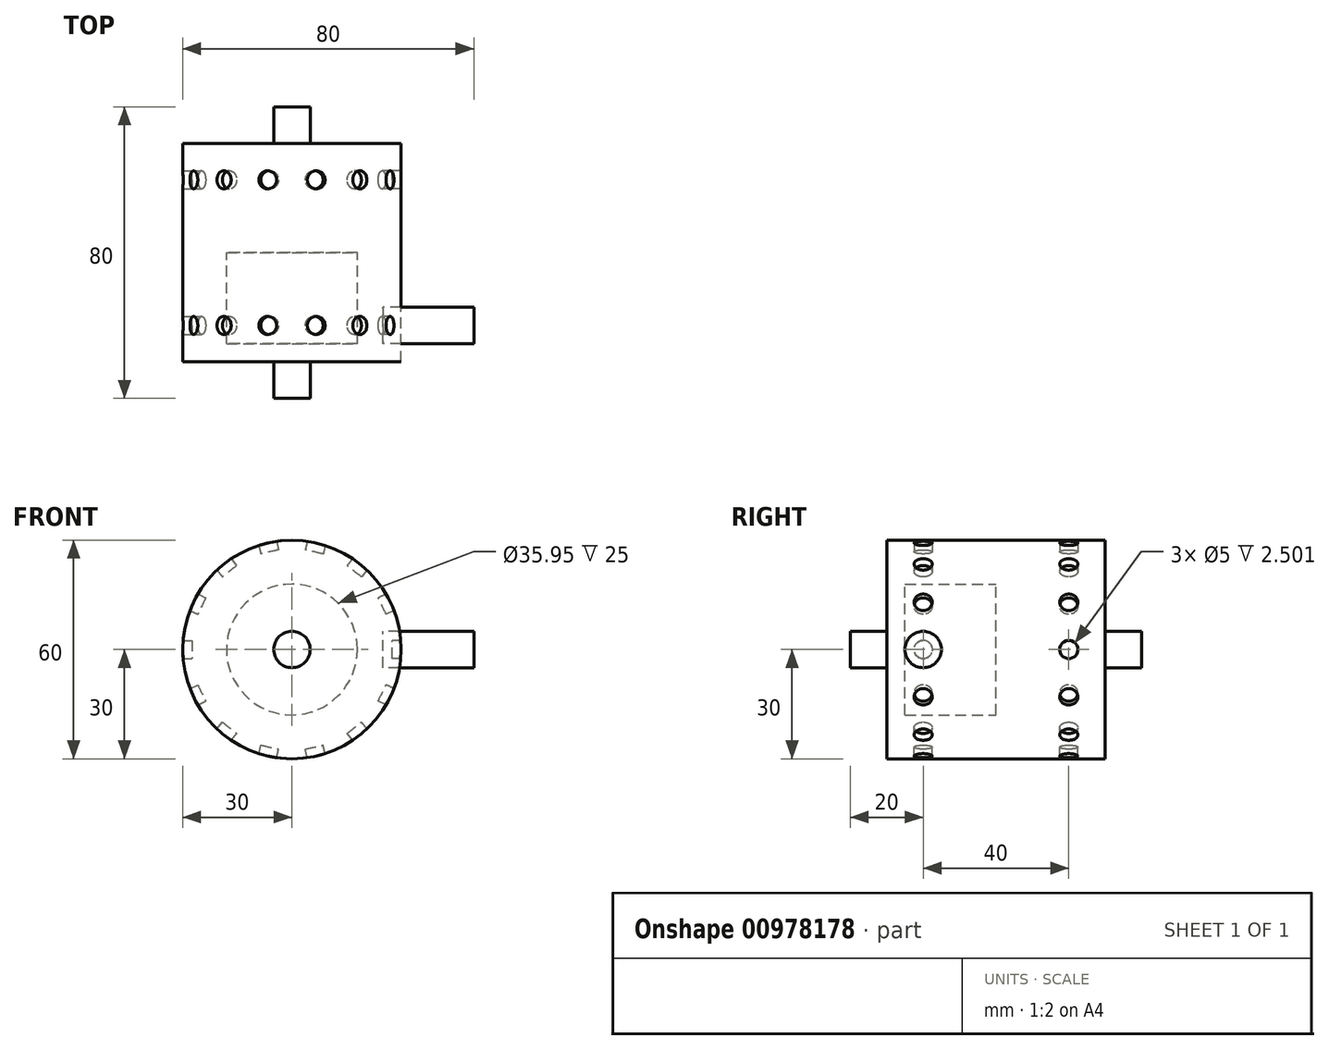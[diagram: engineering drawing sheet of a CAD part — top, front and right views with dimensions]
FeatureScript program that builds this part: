
annotation { "Feature Type Name" : "Feature", "Feature Type Description" : "" }
export const myFeature = defineFeature(function(context is Context, id is Id, definition is map)
    precondition{}
    {
        {
            var Q0;
            Q0=qCreatedBy(makeId("Front.planeOp"),FACE);
            var sketch = newSketch(context, id + "F0", { "sketchPlane" : qUnion([Q0])});
            skCircle(sketch, "E0", {"center": v(0, 0) * mm, "radius": 30 * mm});
            skLineSegment(sketch, "E1", {"start": v(72.87, 0) * mm, "end": v(-75.42, 0) * mm, "construction": true});
            skLineSegment(sketch, "E2", {"start": v(0, -74.84) * mm, "end": v(0, 74.05) * mm, "construction": true});
            skSolve(sketch);
        }
        {
            var Q0;
            Q0 = qSketchRegion(id + "F0", true);
            extrude(context, id + "F1", {"entities" : qUnion([Q0]), "endBound" : BoundingType.SYMMETRIC, "depth" : 60 * mm, "offsetDistance" : 25 * mm});
        }
        {
            var Q0;
            Q0=qCreatedBy(makeId("Right.planeOp"),FACE);
            cPlane(context, id + "F2", {"entities" : qUnion([Q0]), "cplaneType" : CPlaneType.OFFSET, "offset" : 25 * mm, "width" : 150 * mm, "height" : 150 * mm});
        }
        {
            var Q0;
            Q0=qCreatedBy(id+"F2.planeOp",FACE);
            var sketch = newSketch(context, id + "F3", { "sketchPlane" : qUnion([Q0])});
            skCircle(sketch, "E3", {"center": v(-20, 0) * mm, "radius": 5 * mm});
            skCircle(sketch, "E4", {"center": v(20, 0) * mm, "radius": 5 * mm});
            skSolve(sketch);
        }
        {
            var Q0;
            Q0 = qSketchRegion(id + "F3", true);
            extrude(context, id + "F4", {"entities" : qUnion([Q0]), "depth" : 25 * mm, "offsetDistance" : 25 * mm});
        }
        {
            var Q0;
            Q0=makeQuery(id+"F4.opExtrude","SWEPT_BODY",BODY,{"disambiguationData":[OSD([sQuery(id+"F3.wireOp",EDGE,"E3")])]});
            var Q1;
            Q1=makeQuery(id+"F4.opExtrude","SWEPT_BODY",BODY,{"disambiguationData":[OSD([sQuery(id+"F3.wireOp",EDGE,"E4")])]});
            var Q2;
            Q2=makeQuery(id+"F1.opExtrude","CAP_EDGE",EDGE,{"disambiguationData":[OSD([sQuery(id+"F0.wireOp",EDGE,"E0")])],"isStart":true});
            circularPattern(context, id + "F5", {"entities" : qUnion([Q0, Q1]), "axis" : qUnion([Q2]), "angle" : 360 * degree, "instanceCount" : 14, "equalSpace" : true});
        }
        {
            var Q0;
            Q0=makeQuery(id+"F5.opPattern","COPY",BODY,{"derivedFrom":makeQuery(id+"F4.opExtrude","SWEPT_BODY",BODY,{"disambiguationData":[OSD([sQuery(id+"F3.wireOp",EDGE,"E3")])]}),"instanceName":"6"});
            var Q1;
            Q1=makeQuery(id+"F5.opPattern","COPY",BODY,{"derivedFrom":makeQuery(id+"F4.opExtrude","SWEPT_BODY",BODY,{"disambiguationData":[OSD([sQuery(id+"F3.wireOp",EDGE,"E3")])]}),"instanceName":"7"});
            var Q2;
            Q2=makeQuery(id+"F5.opPattern","COPY",BODY,{"derivedFrom":makeQuery(id+"F4.opExtrude","SWEPT_BODY",BODY,{"disambiguationData":[OSD([sQuery(id+"F3.wireOp",EDGE,"E3")])]}),"instanceName":"8"});
            var Q3;
            Q3=makeQuery(id+"F5.opPattern","COPY",BODY,{"derivedFrom":makeQuery(id+"F4.opExtrude","SWEPT_BODY",BODY,{"disambiguationData":[OSD([sQuery(id+"F3.wireOp",EDGE,"E3")])]}),"instanceName":"9"});
            var Q4;
            Q4=makeQuery(id+"F5.opPattern","COPY",BODY,{"derivedFrom":makeQuery(id+"F4.opExtrude","SWEPT_BODY",BODY,{"disambiguationData":[OSD([sQuery(id+"F3.wireOp",EDGE,"E3")])]}),"instanceName":"10"});
            var Q5;
            Q5=makeQuery(id+"F5.opPattern","COPY",BODY,{"derivedFrom":makeQuery(id+"F4.opExtrude","SWEPT_BODY",BODY,{"disambiguationData":[OSD([sQuery(id+"F3.wireOp",EDGE,"E3")])]}),"instanceName":"11"});
            var Q6;
            Q6=makeQuery(id+"F5.opPattern","COPY",BODY,{"derivedFrom":makeQuery(id+"F4.opExtrude","SWEPT_BODY",BODY,{"disambiguationData":[OSD([sQuery(id+"F3.wireOp",EDGE,"E3")])]}),"instanceName":"12"});
            var Q7;
            Q7=makeQuery(id+"F5.opPattern","COPY",BODY,{"derivedFrom":makeQuery(id+"F4.opExtrude","SWEPT_BODY",BODY,{"disambiguationData":[OSD([sQuery(id+"F3.wireOp",EDGE,"E3")])]}),"instanceName":"13"});
            var Q8;
            Q8=makeQuery(id+"F5.opPattern","COPY",BODY,{"derivedFrom":makeQuery(id+"F4.opExtrude","SWEPT_BODY",BODY,{"disambiguationData":[OSD([sQuery(id+"F3.wireOp",EDGE,"E3")])]}),"instanceName":"1"});
            var Q9;
            Q9=makeQuery(id+"F5.opPattern","COPY",BODY,{"derivedFrom":makeQuery(id+"F4.opExtrude","SWEPT_BODY",BODY,{"disambiguationData":[OSD([sQuery(id+"F3.wireOp",EDGE,"E3")])]}),"instanceName":"2"});
            var Q10;
            Q10=makeQuery(id+"F5.opPattern","COPY",BODY,{"derivedFrom":makeQuery(id+"F4.opExtrude","SWEPT_BODY",BODY,{"disambiguationData":[OSD([sQuery(id+"F3.wireOp",EDGE,"E3")])]}),"instanceName":"3"});
            var Q11;
            Q11=makeQuery(id+"F5.opPattern","COPY",BODY,{"derivedFrom":makeQuery(id+"F4.opExtrude","SWEPT_BODY",BODY,{"disambiguationData":[OSD([sQuery(id+"F3.wireOp",EDGE,"E3")])]}),"instanceName":"4"});
            var Q12;
            Q12=makeQuery(id+"F5.opPattern","COPY",BODY,{"derivedFrom":makeQuery(id+"F4.opExtrude","SWEPT_BODY",BODY,{"disambiguationData":[OSD([sQuery(id+"F3.wireOp",EDGE,"E3")])]}),"instanceName":"5"});
            var Q13;
            Q13=makeQuery(id+"F5.opPattern","COPY",BODY,{"derivedFrom":makeQuery(id+"F4.opExtrude","SWEPT_BODY",BODY,{"disambiguationData":[OSD([sQuery(id+"F3.wireOp",EDGE,"E4")])]}),"instanceName":"2"});
            var Q14;
            Q14=makeQuery(id+"F5.opPattern","COPY",BODY,{"derivedFrom":makeQuery(id+"F4.opExtrude","SWEPT_BODY",BODY,{"disambiguationData":[OSD([sQuery(id+"F3.wireOp",EDGE,"E4")])]}),"instanceName":"3"});
            var Q15;
            Q15=makeQuery(id+"F5.opPattern","COPY",BODY,{"derivedFrom":makeQuery(id+"F4.opExtrude","SWEPT_BODY",BODY,{"disambiguationData":[OSD([sQuery(id+"F3.wireOp",EDGE,"E4")])]}),"instanceName":"4"});
            var Q16;
            Q16=makeQuery(id+"F5.opPattern","COPY",BODY,{"derivedFrom":makeQuery(id+"F4.opExtrude","SWEPT_BODY",BODY,{"disambiguationData":[OSD([sQuery(id+"F3.wireOp",EDGE,"E4")])]}),"instanceName":"5"});
            var Q17;
            Q17=makeQuery(id+"F5.opPattern","COPY",BODY,{"derivedFrom":makeQuery(id+"F4.opExtrude","SWEPT_BODY",BODY,{"disambiguationData":[OSD([sQuery(id+"F3.wireOp",EDGE,"E4")])]}),"instanceName":"6"});
            var Q18;
            Q18=makeQuery(id+"F5.opPattern","COPY",BODY,{"derivedFrom":makeQuery(id+"F4.opExtrude","SWEPT_BODY",BODY,{"disambiguationData":[OSD([sQuery(id+"F3.wireOp",EDGE,"E4")])]}),"instanceName":"7"});
            var Q19;
            Q19=makeQuery(id+"F5.opPattern","COPY",BODY,{"derivedFrom":makeQuery(id+"F4.opExtrude","SWEPT_BODY",BODY,{"disambiguationData":[OSD([sQuery(id+"F3.wireOp",EDGE,"E4")])]}),"instanceName":"8"});
            var Q20;
            Q20=makeQuery(id+"F5.opPattern","COPY",BODY,{"derivedFrom":makeQuery(id+"F4.opExtrude","SWEPT_BODY",BODY,{"disambiguationData":[OSD([sQuery(id+"F3.wireOp",EDGE,"E4")])]}),"instanceName":"9"});
            var Q21;
            Q21=makeQuery(id+"F5.opPattern","COPY",BODY,{"derivedFrom":makeQuery(id+"F4.opExtrude","SWEPT_BODY",BODY,{"disambiguationData":[OSD([sQuery(id+"F3.wireOp",EDGE,"E4")])]}),"instanceName":"10"});
            var Q22;
            Q22=makeQuery(id+"F5.opPattern","COPY",BODY,{"derivedFrom":makeQuery(id+"F4.opExtrude","SWEPT_BODY",BODY,{"disambiguationData":[OSD([sQuery(id+"F3.wireOp",EDGE,"E4")])]}),"instanceName":"11"});
            var Q23;
            Q23=makeQuery(id+"F5.opPattern","COPY",BODY,{"derivedFrom":makeQuery(id+"F4.opExtrude","SWEPT_BODY",BODY,{"disambiguationData":[OSD([sQuery(id+"F3.wireOp",EDGE,"E4")])]}),"instanceName":"12"});
            var Q24;
            Q24=makeQuery(id+"F5.opPattern","COPY",BODY,{"derivedFrom":makeQuery(id+"F4.opExtrude","SWEPT_BODY",BODY,{"disambiguationData":[OSD([sQuery(id+"F3.wireOp",EDGE,"E4")])]}),"instanceName":"13"});
            var Q25;
            Q25=makeQuery(id+"F4.opExtrude","SWEPT_BODY",BODY,{"disambiguationData":[OSD([sQuery(id+"F3.wireOp",EDGE,"E4")])]});
            var Q26;
            Q26=makeQuery(id+"F5.opPattern","COPY",BODY,{"derivedFrom":makeQuery(id+"F4.opExtrude","SWEPT_BODY",BODY,{"disambiguationData":[OSD([sQuery(id+"F3.wireOp",EDGE,"E4")])]}),"instanceName":"1"});
            var Q27;
            Q27=makeQuery(id+"F1.opExtrude","SWEPT_BODY",BODY,{"disambiguationData":[OSD([sQuery(id+"F0.wireOp",EDGE,"E0")])]});
            booleanBodies(context, id + "F6", {"operationType" : BooleanOperationType.SUBTRACTION, "tools" : qUnion([Q0, Q1, Q2, Q3, Q4, Q5, Q6, Q7, Q8, Q9, Q10, Q11, Q12, Q13, Q14, Q15, Q16, Q17, Q18, Q19, Q20, Q21, Q22, Q23, Q24, Q25, Q26]), "targets" : qUnion([Q27]), "offset" : true, "offsetAll" : true, "offsetDistance" : 2.5 * mm, "oppositeDirection" : true});
        }
        {
            var Q0;
            Q0=qCreatedBy(makeId("Front.planeOp"),FACE);
            var sketch = newSketch(context, id + "F7", { "sketchPlane" : qUnion([Q0])});
            skCircle(sketch, "E5", {"center": v(0, 0) * mm, "radius": 5 * mm});
            skSolve(sketch);
        }
        {
            var Q0;
            Q0 = qSketchRegion(id + "F7", true);
            extrude(context, id + "F8", {"entities" : qUnion([Q0]), "operationType" : NewBodyOperationType.ADD, "endBound" : BoundingType.SYMMETRIC, "depth" : 80 * mm, "offsetDistance" : 25 * mm});
        }
        {
            var Q0;
            Q0=qCreatedBy(makeId("Front.planeOp"),FACE);
            var sketch = newSketch(context, id + "F9", { "sketchPlane" : qUnion([Q0])});
            skCircle(sketch, "E6", {"center": v(0, 0) * mm, "radius": 17.97 * mm});
            skSolve(sketch);
        }
        {
            var Q0;
            Q0 = qSketchRegion(id + "F9", true);
            extrude(context, id + "F10", {"entities" : qUnion([Q0]), "operationType" : NewBodyOperationType.REMOVE, "depth" : 25 * mm, "offsetDistance" : 25 * mm});
        }
    });
